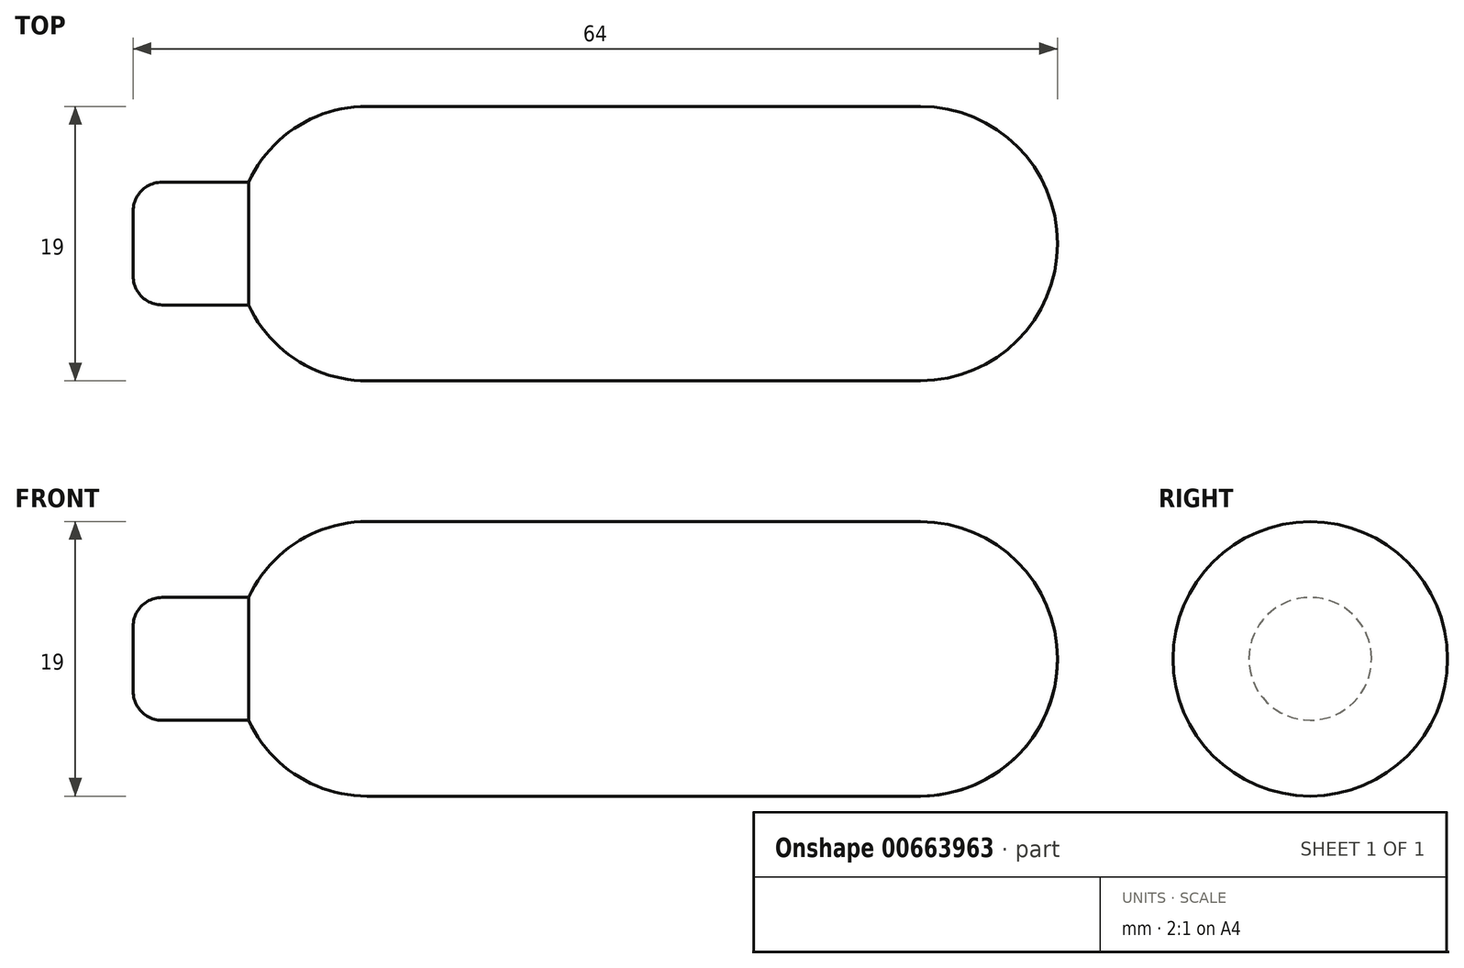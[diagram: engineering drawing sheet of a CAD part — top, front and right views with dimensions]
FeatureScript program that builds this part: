
annotation { "Feature Type Name" : "Feature", "Feature Type Description" : "" }
export const myFeature = defineFeature(function(context is Context, id is Id, definition is map)
    precondition{}
    {
        {
            var Q0;
            Q0=qCreatedBy(makeId("Front.planeOp"),FACE);
            var sketch = newSketch(context, id + "F0", { "sketchPlane" : qUnion([Q0])});
            skLineSegment(sketch, "E0", {"start": v(0, 0) * mm, "end": v(64, 0) * mm});
            skLineSegment(sketch, "E1", {"start": v(0, 0) * mm, "end": v(0, 4.25) * mm});
            skLineSegment(sketch, "E2", {"start": v(0, 4.25) * mm, "end": v(8, 4.25) * mm});
            skLineSegment(sketch, "E3", {"start": v(8, 4.25) * mm, "end": v(8, 9.5) * mm});
            skLineSegment(sketch, "E4", {"start": v(8, 9.5) * mm, "end": v(64, 9.5) * mm});
            skLineSegment(sketch, "E5", {"start": v(64, 9.5) * mm, "end": v(64, 0) * mm});
            skSolve(sketch);
        }
        {
            var Q0;
            Q0 = qSketchRegion(id + "F0", true);
            var Q1;
            Q1=sQuery(id+"F0.wireOp",EDGE,"E0");
            revolve(context, id + "F1", {"entities" : qUnion([Q0]), "axis" : qUnion([Q1]), "revolveType" : RevolveType.FULL});
        }
        {
            var Q0;
            Q0=makeQuery(id+"F1.opRevolve","SWEPT_EDGE",EDGE,{"disambiguationData":[OSD([sQuery(id+"F0.wireOp",EDGE,"E4"),sQuery(id+"F0.wireOp",EDGE,"E5")])]});
            fillet(context, id + "F2", {"entities" : qUnion([Q0]), "radius" : 9.5 * mm, "tangentPropagation" : true, "allowEdgeOverflow" : false});
        }
        {
            var Q0;
            Q0=makeQuery(id+"F1.opRevolve","SWEPT_EDGE",EDGE,{"disambiguationData":[OSD([sQuery(id+"F0.wireOp",EDGE,"E3"),sQuery(id+"F0.wireOp",EDGE,"E4")])]});
            fillet(context, id + "F3", {"entities" : qUnion([Q0]), "radius" : 9 * mm, "tangentPropagation" : true, "allowEdgeOverflow" : false});
        }
        {
            var Q0;
            Q0=makeQuery(id+"F1.opRevolve","SWEPT_EDGE",EDGE,{"disambiguationData":[OSD([sQuery(id+"F0.wireOp",EDGE,"E1"),sQuery(id+"F0.wireOp",EDGE,"E2")])]});
            fillet(context, id + "F4", {"entities" : qUnion([Q0]), "radius" : 2 * mm, "tangentPropagation" : true, "allowEdgeOverflow" : false});
        }
    });
